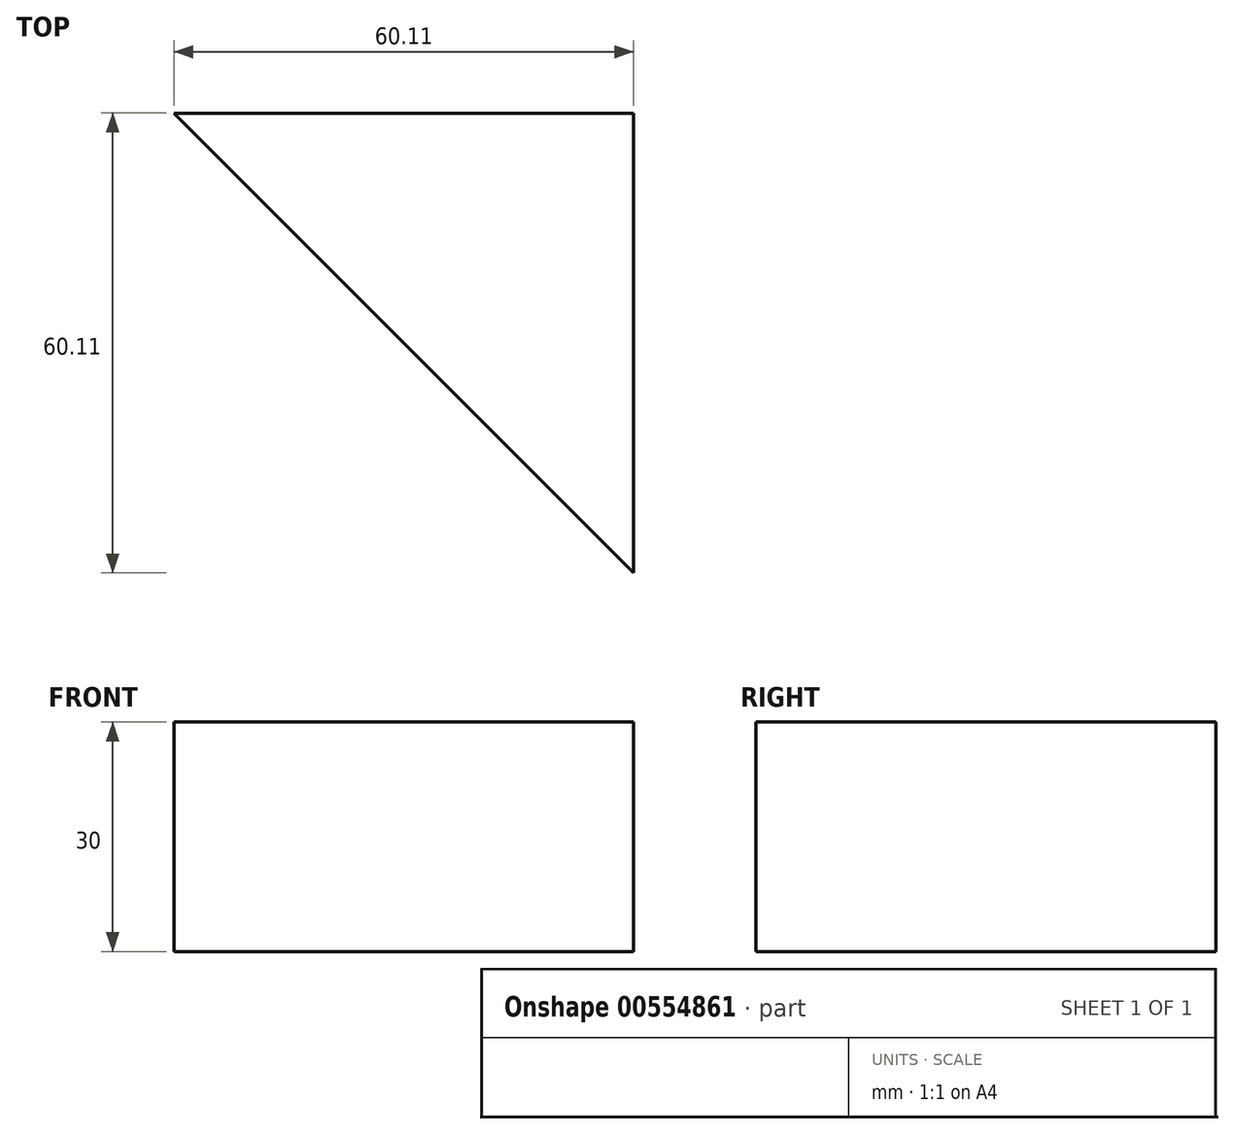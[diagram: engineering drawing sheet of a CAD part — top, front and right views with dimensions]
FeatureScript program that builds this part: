
annotation { "Feature Type Name" : "Feature", "Feature Type Description" : "" }
export const myFeature = defineFeature(function(context is Context, id is Id, definition is map)
    precondition{}
    {
        {
            var Q0;
            Q0=qCreatedBy(makeId("Top.planeOp"),FACE);
            var sketch = newSketch(context, id + "F0", { "sketchPlane" : qUnion([Q0])});
            skLineSegment(sketch, "E0", {"start": v(-49.28, 49.9) * mm, "end": v(10.83, 49.9) * mm});
            skLineSegment(sketch, "E1", {"start": v(10.83, 49.9) * mm, "end": v(10.83, -10.2) * mm});
            skLineSegment(sketch, "E2", {"start": v(10.83, -10.2) * mm, "end": v(-49.28, 49.9) * mm});
            skSolve(sketch);
        }
        {
            var Q0;
            Q0=makeQuery(id+"F0.imprint","IMPRINT",FACE,{"disambiguationData":[TD([[makeQuery(id+"F0.imprint","IMPRINT",EDGE,{"derivedFrom":sQuery(id+"F0.wireOp",EDGE,"E0")}),-1.0]])]});
            extrude(context, id + "F1", {"entities" : qUnion([Q0]), "depth" : 30 * mm, "offsetDistance" : 25 * mm});
        }
    });
